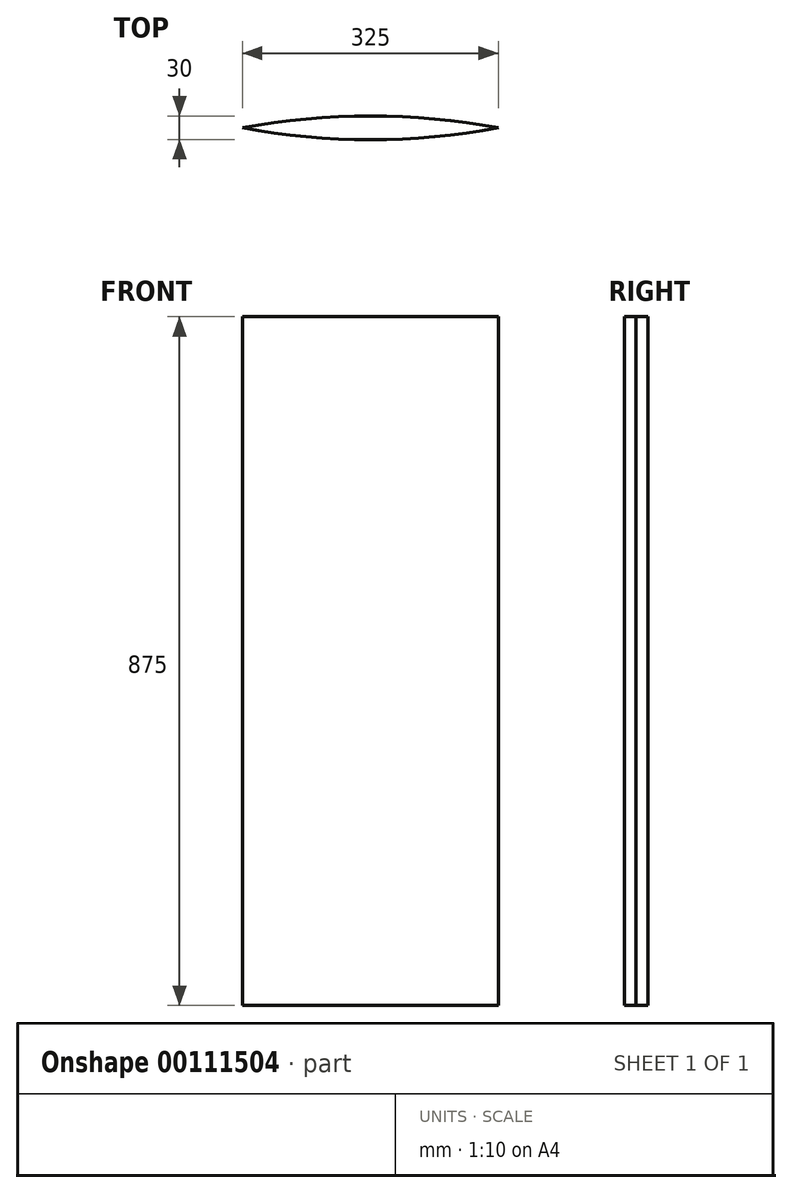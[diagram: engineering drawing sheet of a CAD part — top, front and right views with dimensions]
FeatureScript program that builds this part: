
annotation { "Feature Type Name" : "Feature", "Feature Type Description" : "" }
export const myFeature = defineFeature(function(context is Context, id is Id, definition is map)
    precondition{}
    {
        {
            var Q0;
            Q0=qCreatedBy(makeId("Top.planeOp"),FACE);
            var sketch = newSketch(context, id + "F0", { "sketchPlane" : qUnion([Q0])});
            skLineSegment(sketch, "E0", {"start": v(-167.42, 0) * mm, "end": v(157.58, 0) * mm});
            skArc(sketch, "E1", {"start": v(157.58, 0) * mm, "mid": v(-4.92, 15) * mm, "end": v(-167.42, 0) * mm});
            skArc(sketch, "E2.MirrorCS", {"start": v(157.58, 0) * mm, "mid": v(-4.92, -15) * mm, "end": v(-167.42, 0) * mm});
            skSolve(sketch);
        }
        {
            var Q0;
            Q0=makeQuery(id+"F0.imprint","IMPRINT",FACE,{"disambiguationData":[TD([[makeQuery(id+"F0.imprint","IMPRINT",EDGE,{"derivedFrom":sQuery(id+"F0.wireOp",EDGE,"E0")}),1.0]])]});
            var Q1;
            Q1=makeQuery(id+"F0.imprint","IMPRINT",FACE,{"disambiguationData":[TD([[makeQuery(id+"F0.imprint","IMPRINT",EDGE,{"derivedFrom":sQuery(id+"F0.wireOp",EDGE,"E0")}),-1.0]])]});
            extrude(context, id + "F1", {"entities" : qUnion([Q0, Q1]), "endBound" : BoundingType.SYMMETRIC, "depth" : 875 * mm});
        }
    });
